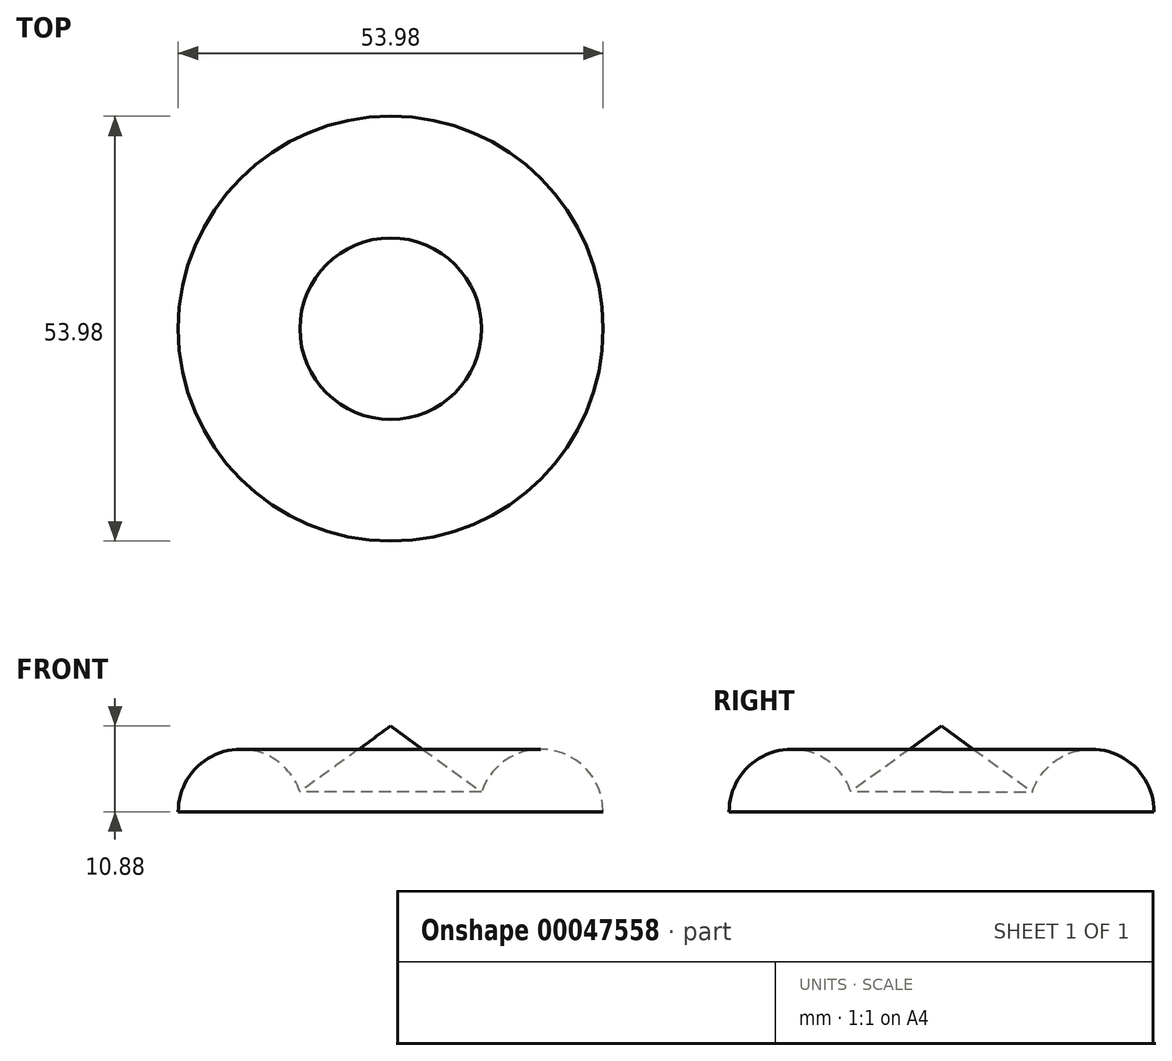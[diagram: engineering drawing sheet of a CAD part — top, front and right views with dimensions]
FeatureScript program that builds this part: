
annotation { "Feature Type Name" : "Feature", "Feature Type Description" : "" }
export const myFeature = defineFeature(function(context is Context, id is Id, definition is map)
    precondition{}
    {
        {
            var Q0;
            Q0=qCreatedBy(makeId("Front.planeOp"),FACE);
            var sketch = newSketch(context, id + "F0", { "sketchPlane" : qUnion([Q0])});
            skLineSegment(sketch, "E0", {"start": v(0, 25.03) * mm, "end": v(0, -15.1) * mm});
            skLineSegment(sketch, "E1", {"start": v(0, 25.03) * mm, "end": v(2.54, 25.03) * mm, "construction": true});
            skLineSegment(sketch, "E2", {"start": v(2.54, 25.03) * mm, "end": v(2.54, 2.54) * mm, "construction": true});
            skLineSegment(sketch, "E3", {"start": v(2.54, 2.54) * mm, "end": v(11.11, 2.54) * mm, "construction": true});
            skArc(sketch, "E4", {"start": v(26.99, 2.54) * mm, "mid": v(19.05, 10.48) * mm, "end": v(11.11, 2.54) * mm, "construction": true});
            skLineSegment(sketch, "E5", {"start": v(26.99, 2.54) * mm, "end": v(26.99, 0) * mm, "construction": true});
            skLineSegment(sketch, "E6", {"start": v(26.99, 0) * mm, "end": v(0, 0) * mm, "construction": true});
            skArc(sketch, "E7", {"start": v(26.99, 0) * mm, "mid": v(20.34, 7.83) * mm, "end": v(11.53, 2.54) * mm});
            skLineSegment(sketch, "E8", {"start": v(11.53, 2.54) * mm, "end": v(0, 10.88) * mm});
            skLineSegment(sketch, "E9", {"start": v(0, 10.88) * mm, "end": v(0, 0) * mm});
            skLineSegment(sketch, "E10", {"start": v(0, 0) * mm, "end": v(26.99, 0) * mm});
            skLineSegment(sketch, "E11", {"start": v(0, 10.88) * mm, "end": v(0, 37.11) * mm});
            skSolve(sketch);
        }
        {
            var Q0;
            Q0=makeQuery(id+"F0.imprint","IMPRINT",FACE,{"disambiguationData":[TD([[makeQuery(id+"F0.imprint","IMPRINT",EDGE,{"derivedFrom":sQuery(id+"F0.wireOp",EDGE,"E7")}),1.0]])]});
            var Q1;
            Q1=sQuery(id+"F0.wireOp",EDGE,"E0");
            revolve(context, id + "F1", {"entities" : qUnion([Q0]), "axis" : qUnion([Q1]), "revolveType" : RevolveType.FULL});
        }
    });
